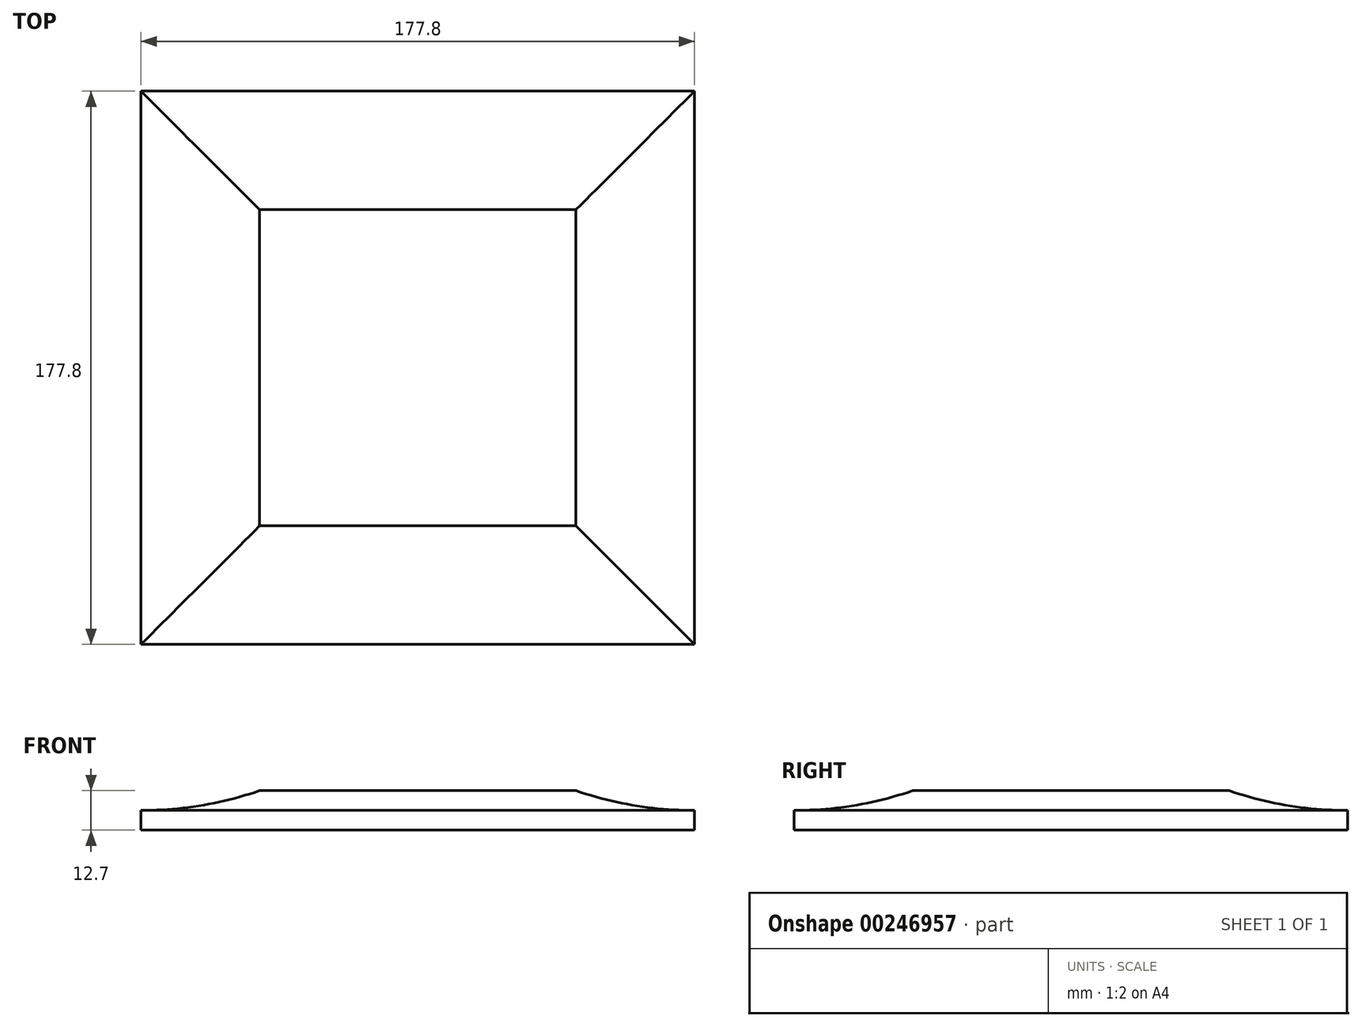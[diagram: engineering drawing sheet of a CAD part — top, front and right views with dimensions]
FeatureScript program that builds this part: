
annotation { "Feature Type Name" : "Feature", "Feature Type Description" : "" }
export const myFeature = defineFeature(function(context is Context, id is Id, definition is map)
    precondition{}
    {
        {
            var Q0;
            Q0=qCreatedBy(makeId("Top.planeOp"),FACE);
            var sketch = newSketch(context, id + "F0", { "sketchPlane" : qUnion([Q0])});
            skLineSegment(sketch, "E0.bottom", {"start": v(88.9, -88.9) * mm, "end": v(-88.9, -88.9) * mm});
            skLineSegment(sketch, "E0.top", {"start": v(88.9, 88.9) * mm, "end": v(-88.9, 88.9) * mm});
            skLineSegment(sketch, "E0.left", {"start": v(88.9, -88.9) * mm, "end": v(88.9, 88.9) * mm});
            skLineSegment(sketch, "E0.right", {"start": v(-88.9, -88.9) * mm, "end": v(-88.9, 88.9) * mm});
            skPoint(sketch, "E0.middle", {"position": v(0, 0) * mm});
            skSolve(sketch);
        }
        {
            var Q0;
            Q0=qCreatedBy(makeId("Front.planeOp"),FACE);
            var sketch = newSketch(context, id + "F1", { "sketchPlane" : qUnion([Q0])});
            skPoint(sketch, "E1.0", {"position": v(88.9, 0) * mm});
            skLineSegment(sketch, "E2", {"start": v(0, 0) * mm, "end": v(88.9, 0) * mm});
            skLineSegment(sketch, "E3", {"start": v(88.9, 0) * mm, "end": v(88.9, 6.35) * mm});
            skLineSegment(sketch, "E4", {"start": v(88.9, 6.35) * mm, "end": v(106.31, 6.35) * mm, "construction": true});
            skLineSegment(sketch, "E5", {"start": v(0, 0) * mm, "end": v(0, 12.7) * mm});
            skLineSegment(sketch, "E6", {"start": v(0, 12.7) * mm, "end": v(50.8, 12.7) * mm});
            skArc(sketch, "E7", {"start": v(88.9, 6.35) * mm, "mid": v(69.59, 7.95) * mm, "end": v(50.8, 12.7) * mm});
            skSolve(sketch);
        }
        {
            var Q0;
            Q0=makeQuery(id+"F1.imprint","IMPRINT",FACE,{"disambiguationData":[TD([[makeQuery(id+"F1.imprint","IMPRINT",EDGE,{"derivedFrom":sQuery(id+"F1.wireOp",EDGE,"E2")}),1.0]])]});
            var Q1;
            Q1=sQuery(id+"F0.wireOp",EDGE,"E0.left");
            var Q2;
            Q2=sQuery(id+"F0.wireOp",EDGE,"E0.top");
            var Q3;
            Q3=sQuery(id+"F0.wireOp",EDGE,"E0.right");
            var Q4;
            Q4=sQuery(id+"F0.wireOp",EDGE,"E0.bottom");
            sweep(context, id + "F2", {"profiles" : qUnion([Q0]), "path" : qUnion([Q1, Q2, Q3, Q4])});
        }
    });
